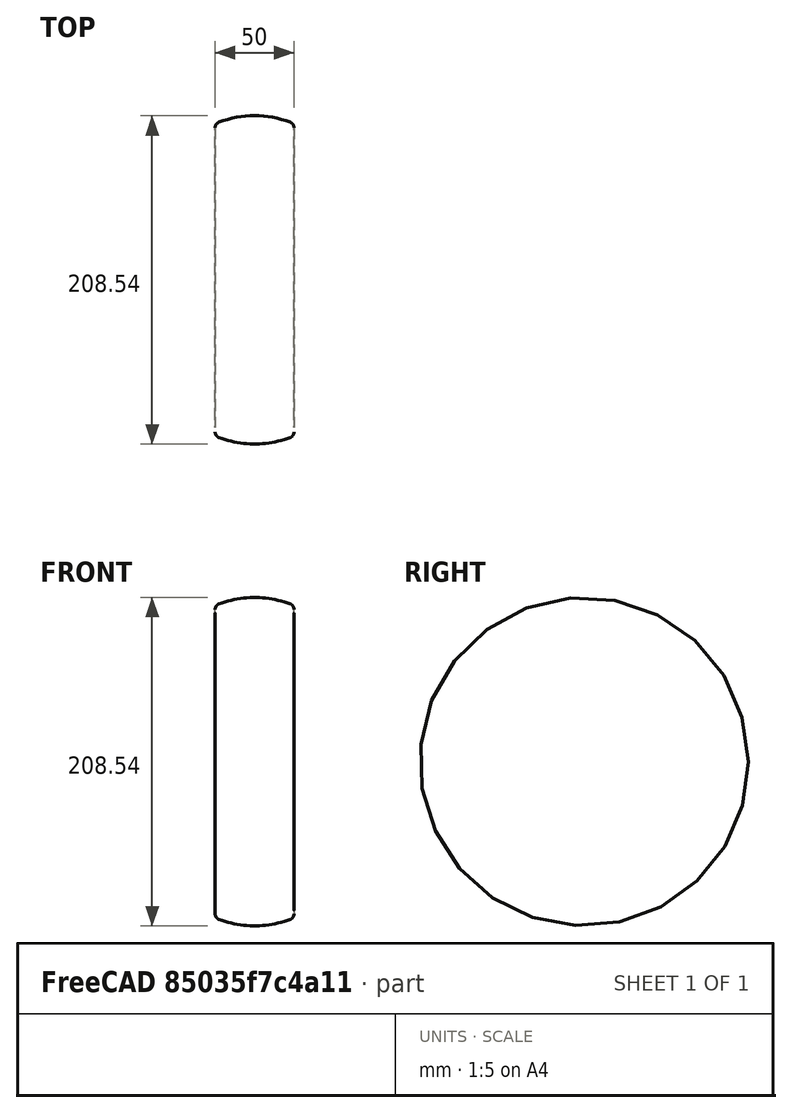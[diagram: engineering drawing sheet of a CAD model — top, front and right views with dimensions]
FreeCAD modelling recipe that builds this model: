
FCSTD DOCUMENT
Label: gyuru_volume_test_p3_tomor
objects: Sketcher::SketchObject×1, Part::Revolution×1
note: 2 computed .brp shape members not serialized (recipe doc carries the construction recipe); baked Part::Feature solids carry a one-line shape summary decoded from their .brp

FEATURE [Sketcher::SketchObject] Sketch
  sketch-geometry (7):
    g0: LineSegment StartX=50 StartY=96.7703 StartZ=0 EndX=50 EndY=0 EndZ=0
    g1: LineSegment [constr] StartX=-21.5219 StartY=104.27 StartZ=0 EndX=96.4869 EndY=104.27 EndZ=0
    g2: ArcOfCircle CenterX=25 CenterY=40.47 CenterZ=0 NormalX=0 NormalY=0 NormalZ=1 Radius=63.8 StartAngle=1.20683 EndAngle=1.93476
    g3: ArcOfCircle CenterX=3.553 CenterY=96.7703 CenterZ=0 NormalX=0 NormalY=0 NormalZ=1 Radius=3.553 StartAngle=1.93476 EndAngle=3.14159
    g4: ArcOfCircle CenterX=46.447 CenterY=96.7703 CenterZ=0 NormalX=0 NormalY=0 NormalZ=1 Radius=3.553 StartAngle=6.28319 EndAngle=7.49001
    g5: LineSegment StartX=0 StartY=96.7703 StartZ=0 EndX=0 EndY=0 EndZ=0
    g6: LineSegment StartX=0 StartY=0 StartZ=0 EndX=50 EndY=0 EndZ=0
  constraints (24):
    c: Vertical(g0)
    c: DistanceX(g0) = 50
    c: Horizontal(g1)
    c: DistanceY(g1) = 104.27
    c: Radius(g2) = 63.8
    c: Tangent(g2,g1)
    c: DistanceX(g2) = 25
    c: Tangent(g3,g2)
    c: Tangent(g2,g4)
    c: Tangent(g4,g0)
    c: PointOnObject(g5,g-2)
    c: PointOnObject(g5,g-2)
    c: Tangent(g5,g3)
    c: Radius(g3) = 3.553
    c: Radius(g4) = 3.553
    c: DistanceX(g3) = 0
    c: DistanceX(g4) = 50
    c: Coincident(g4,g0)
    c: Coincident(g5,g3)
    c: PointOnObject(g0,g-1)
    c: PointOnObject(g5,g-1)
    c: Coincident(g6,g-1)
    c: Coincident(g6,g0)
    c: Horizontal(g6)
FEATURE [Part::Revolution] Revolve
  Angle = 360
  Axis = (1,0,0)
  Base = (0,0,0)
  Placement = pos=(10.8789,302.175,9.24572) rot=(0,0,1;0rad)
  Source = -> Sketch
